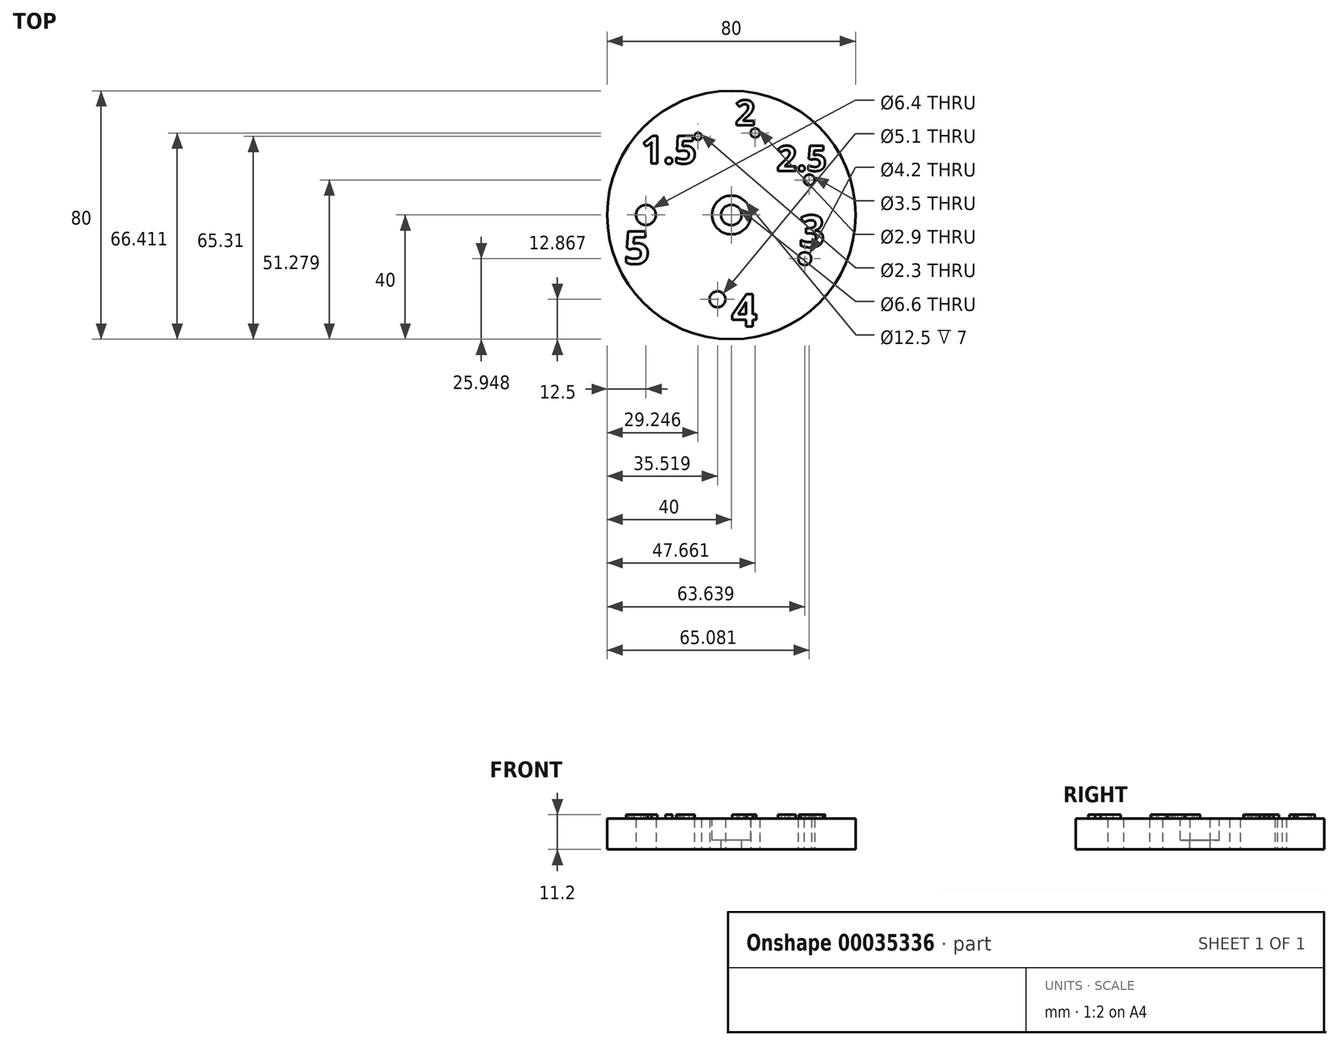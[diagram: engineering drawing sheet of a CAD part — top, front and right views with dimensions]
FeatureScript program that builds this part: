
annotation { "Feature Type Name" : "Feature", "Feature Type Description" : "" }
export const myFeature = defineFeature(function(context is Context, id is Id, definition is map)
    precondition{}
    {
        {
            var Q0;
            Q0=qCreatedBy(makeId("Top.planeOp"),FACE);
            var sketch = newSketch(context, id + "F0", { "sketchPlane" : qUnion([Q0])});
            skCircle(sketch, "E0", {"center": v(0, 0) * mm, "radius": 40 * mm});
            skCircle(sketch, "E1", {"center": v(0, 0) * mm, "radius": 27.5 * mm, "construction": true});
            skCircle(sketch, "E2", {"center": v(-27.5, 0) * mm, "radius": 3.2 * mm});
            skCircle(sketch, "E3", {"center": v(-4.48, -27.13) * mm, "radius": 2.55 * mm});
            skCircle(sketch, "E4", {"center": v(23.64, -14.05) * mm, "radius": 2.1 * mm});
            skCircle(sketch, "E5", {"center": v(25.08, 11.28) * mm, "radius": 1.75 * mm});
            skCircle(sketch, "E6", {"center": v(7.66, 26.41) * mm, "radius": 1.45 * mm});
            skCircle(sketch, "E7", {"center": v(-10.75, 25.31) * mm, "radius": 1.15 * mm});
            skCircle(sketch, "E8", {"center": v(-27.5, 0) * mm, "radius": 13 * mm, "construction": true});
            skCircle(sketch, "E9", {"center": v(-4.48, -27.13) * mm, "radius": 13 * mm, "construction": true});
            skCircle(sketch, "E10", {"center": v(23.64, -14.05) * mm, "radius": 10 * mm, "construction": true});
            skCircle(sketch, "E11", {"center": v(25.08, 11.28) * mm, "radius": 8 * mm, "construction": true});
            skSolve(sketch);
        }
        {
            var Q0;
            Q0 = qSketchRegion(id + "F0", true);
            extrude(context, id + "F1", {"entities" : qUnion([Q0]), "depth" : 10 * mm});
        }
        {
            var Q0;
            Q0=makeQuery(id+"F1.opExtrude","CAP_FACE",FACE,{"disambiguationData":[OSD([sQuery(id+"F0.wireOp",EDGE,"E0"),sQuery(id+"F0.wireOp",EDGE,"E2"),sQuery(id+"F0.wireOp",EDGE,"E3"),sQuery(id+"F0.wireOp",EDGE,"E4"),sQuery(id+"F0.wireOp",EDGE,"E5"),sQuery(id+"F0.wireOp",EDGE,"E6"),sQuery(id+"F0.wireOp",EDGE,"E7")])],"isStart":false});
            var sketch = newSketch(context, id + "F2", { "sketchPlane" : qUnion([Q0])});
            skPoint(sketch, "E12", {"position": v(0, 0) * mm});
            skSolve(sketch);
        }
        {
            var Q0;
            Q0=sQuery(id+"F2.wireOp",VERTEX,"E12");
            var Q1;
            Q1=makeQuery(id+"F1.opExtrude","SWEPT_BODY",BODY,{"disambiguationData":[OSD([sQuery(id+"F0.wireOp",EDGE,"E0"),sQuery(id+"F0.wireOp",EDGE,"E2"),sQuery(id+"F0.wireOp",EDGE,"E3"),sQuery(id+"F0.wireOp",EDGE,"E4"),sQuery(id+"F0.wireOp",EDGE,"E5"),sQuery(id+"F0.wireOp",EDGE,"E6"),sQuery(id+"F0.wireOp",EDGE,"E7")])]});
            hole(context, id + "F3", {"style" : HoleStyle.C_BORE, "holeDiameter" : 6.6 * mm, "cBoreDiameter" : 12.5 * mm, "cBoreDepth" : 7 * mm, "endStyle" : HoleEndStyle.THROUGH, "locations" : qUnion([Q0]), "scope" : qUnion([Q1])});
        }
        {
            var Q0;
            Q0=makeQuery(id+"F1.opExtrude","CAP_FACE",FACE,{"disambiguationData":[OSD([sQuery(id+"F0.wireOp",EDGE,"E0"),sQuery(id+"F0.wireOp",EDGE,"E2"),sQuery(id+"F0.wireOp",EDGE,"E3"),sQuery(id+"F0.wireOp",EDGE,"E4"),sQuery(id+"F0.wireOp",EDGE,"E5"),sQuery(id+"F0.wireOp",EDGE,"E6"),sQuery(id+"F0.wireOp",EDGE,"E7")])],"isStart":false});
            var sketch = newSketch(context, id + "F4", { "sketchPlane" : qUnion([Q0])});
            skText(sketch, "E13", { "text": "5", "fontName": "OpenSans-Bold.ttf"});
            skText(sketch, "E14", { "text": "4", "fontName": "OpenSans-Bold.ttf"});
            skText(sketch, "E15", { "text": "3", "fontName": "OpenSans-Bold.ttf"});
            skText(sketch, "E16", { "text": "2.5", "fontName": "OpenSans-Bold.ttf"});
            skText(sketch, "E17", { "text": "2", "fontName": "OpenSans-Bold.ttf"});
            skText(sketch, "E18", { "text": "1.5", "fontName": "OpenSans-Bold.ttf"});
            const initialGuessF4  = {"E13": [-0.03458, -0.01572, 1, 0, 0.01048], "E14": [0, -0.03583, 1, 0, 0.01048], "E15": [0.02186, -0.0103, 1, 0, 0.0103], "E16": [0.0146, 0.0142, 1, 0, 0.00811], "E17": [0.00124, 0.0289, 1, 0, 0.00811], "E18": [-0.029, 0.01656, 1, 0, 0.00896]};
            skSetInitialGuess(sketch, initialGuessF4);
            skSolve(sketch);
        }
        {
            var Q0;
            Q0 = qSketchRegion(id + "F4", true);
            extrude(context, id + "F5", {"entities" : qUnion([Q0]), "operationType" : NewBodyOperationType.ADD, "depth" : 1.2 * mm});
        }
    });
